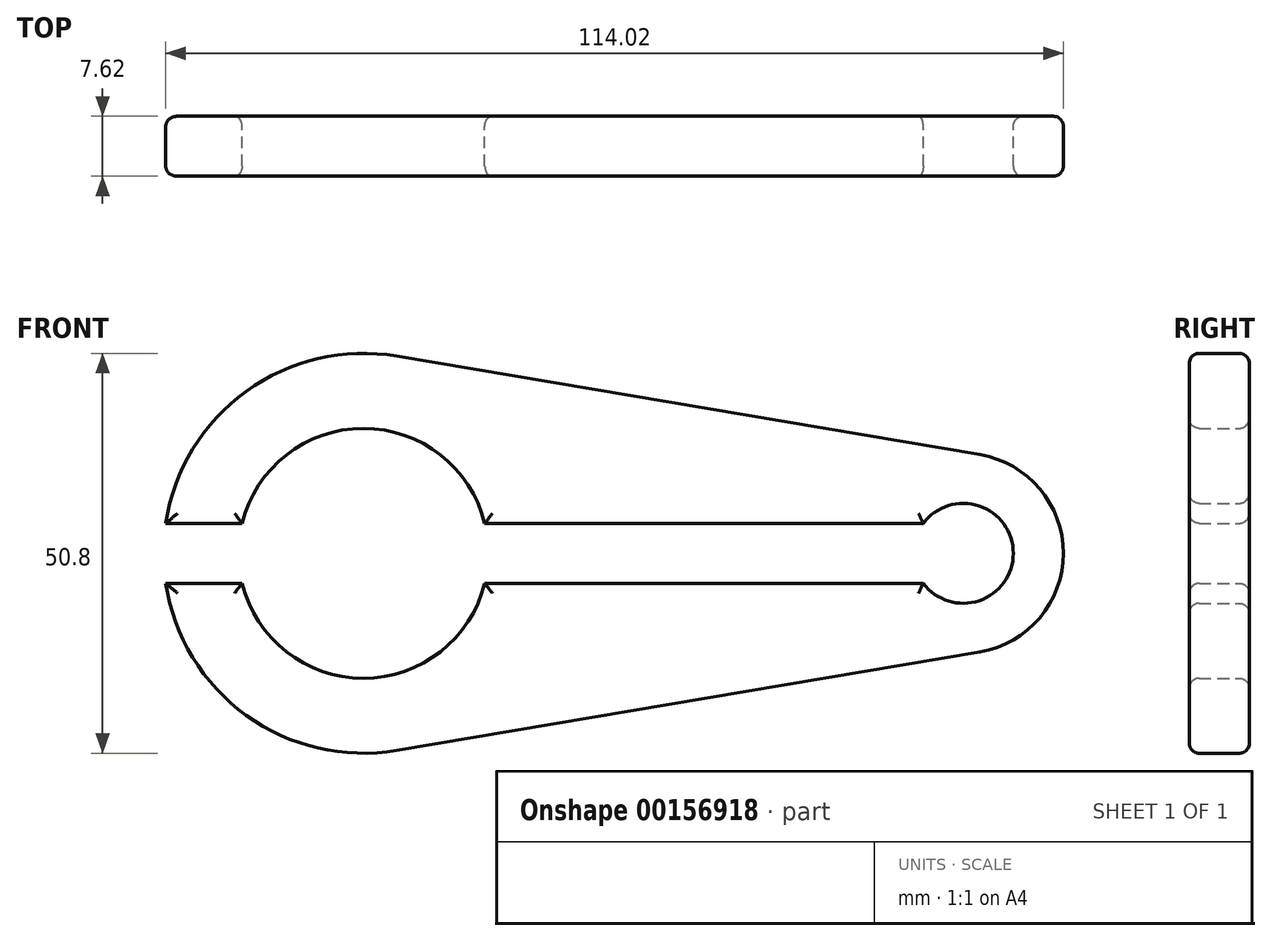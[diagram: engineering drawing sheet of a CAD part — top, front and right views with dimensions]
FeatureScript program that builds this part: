
annotation { "Feature Type Name" : "Feature", "Feature Type Description" : "" }
export const myFeature = defineFeature(function(context is Context, id is Id, definition is map)
    precondition{}
    {
        {
            var Q0;
            Q0=qCreatedBy(makeId("Front.planeOp"),FACE);
            var sketch = newSketch(context, id + "F0", { "sketchPlane" : qUnion([Q0])});
            skArc(sketch, "E0", {"start": v(-27.89, 25.04) * mm, "mid": v(-57.52, 0) * mm, "end": v(-27.89, -25.04) * mm});
            skArc(sketch, "E1", {"start": v(46.2, -12.52) * mm, "mid": v(56.78, 0) * mm, "end": v(46.2, 12.52) * mm});
            skLineSegment(sketch, "E2", {"start": v(-27.89, 25.04) * mm, "end": v(46.2, 12.52) * mm});
            skLineSegment(sketch, "E3", {"start": v(-27.89, -25.04) * mm, "end": v(46.2, -12.52) * mm});
            skSolve(sketch);
        }
        {
            var Q0;
            Q0=qCreatedBy(makeId("Front.planeOp"),FACE);
            var sketch = newSketch(context, id + "F1", { "sketchPlane" : qUnion([Q0])});
            skArc(sketch, "E4", {"start": v(-16.71, 3.81) * mm, "mid": v(-32.12, 15.88) * mm, "end": v(-47.53, 3.81) * mm});
            skLineSegment(sketch, "E5.bottom", {"start": v(-111.96, 3.8) * mm, "end": v(-47.53, 3.8) * mm});
            skLineSegment(sketch, "E5.top", {"start": v(-111.96, -3.81) * mm, "end": v(-47.53, -3.81) * mm});
            skArc(sketch, "E6", {"start": v(39, -3.81) * mm, "mid": v(50.43, 0) * mm, "end": v(39, 3.8) * mm});
            skLineSegment(sketch, "E7", {"start": v(-111.96, 3.8) * mm, "end": v(-111.96, -3.81) * mm});
            skArc(sketch, "E8.trimOffspring", {"start": v(-47.53, -3.8) * mm, "mid": v(-32.12, -15.88) * mm, "end": v(-16.71, -3.8) * mm});
            skLineSegment(sketch, "E9.trimOffspring", {"start": v(-16.71, 3.8) * mm, "end": v(39, 3.8) * mm});
            skLineSegment(sketch, "E10.trimOffspring", {"start": v(-16.71, -3.81) * mm, "end": v(39, -3.81) * mm});
            skSolve(sketch);
        }
        {
            var Q0;
            Q0=makeQuery(id+"F0.imprint","IMPRINT",FACE,{"disambiguationData":[TD([[makeQuery(id+"F0.imprint","IMPRINT",EDGE,{"derivedFrom":sQuery(id+"F0.wireOp",EDGE,"E0")}),1.0]])]});
            extrude(context, id + "F2", {"entities" : qUnion([Q0]), "depth" : 7.62 * mm});
        }
        {
            var Q0;
            Q0=makeQuery(id+"F1.imprint","IMPRINT",FACE,{"disambiguationData":[TD([[makeQuery(id+"F1.imprint","IMPRINT",EDGE,{"derivedFrom":sQuery(id+"F1.wireOp",EDGE,"E4")}),1.0]])]});
            extrude(context, id + "F3", {"entities" : qUnion([Q0]), "operationType" : NewBodyOperationType.REMOVE, "endBound" : BoundingType.THROUGH_ALL, "depth" : 12.7 * mm, "hasSecondDirection" : true, "secondDirectionOppositeDirection" : true, "secondDirectionDepth" : 25.4 * mm});
        }
        {
            var Q0;
            Q0=makeQuery(id+"F2.opExtrude","CAP_FACE",FACE,{"disambiguationData":[OSD([sQuery(id+"F0.wireOp",EDGE,"E0"),sQuery(id+"F0.wireOp",EDGE,"E1"),sQuery(id+"F0.wireOp",EDGE,"E2"),sQuery(id+"F0.wireOp",EDGE,"E3")])],"isStart":true});
            var Q1;
            Q1=makeQuery(id+"F2.opExtrude","CAP_FACE",FACE,{"disambiguationData":[OSD([sQuery(id+"F0.wireOp",EDGE,"E0"),sQuery(id+"F0.wireOp",EDGE,"E1"),sQuery(id+"F0.wireOp",EDGE,"E2"),sQuery(id+"F0.wireOp",EDGE,"E3")])],"isStart":false});
            fillet(context, id + "F4", {"entities" : qUnion([Q0, Q1]), "radius" : 1.27 * mm, "tangentPropagation" : true, "allowEdgeOverflow" : false});
        }
    });
